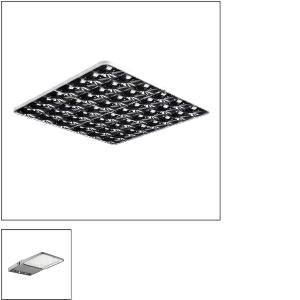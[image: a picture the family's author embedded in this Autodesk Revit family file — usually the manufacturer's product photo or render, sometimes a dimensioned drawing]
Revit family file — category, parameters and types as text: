
# Revit family: siteco_mirrortec_r__indoor___rs05_5nw14093qc_3e65
name_source: partatom
category: Lighting Fixtures
units: mm (PartAtom-declared; Revit-internal decimal feet)

## family parameters
Cut with Voids When Loaded = No
Host = Face
Light Source = No
Part Type = Normal
Room Calculation Point = No
Round Connector Dimension = Use Diameter
Shared = No

## types (1)
- 5XA7682G2H2AC (1 x LED, 33940 lm, 305.7 W, 4000K)
    Apparent Load = 306 VA
    CIE Flux Codes = 47 83 98 53 100
    Color Rendering = 70
    Color Temperature = 4000K
    Default Elevation = 1800 mm
    Description = secondary reflector, for Siteco Mirrortec® Indoor, wire hanger, housing, square, of aluminium, coated, metallic grey (RAL 9006), fresnel reflector 100, of PMMA, aluminized, highly specular, light point resolution, fresnel structure, length: 1.200 mm, width: 1.200 mm

Light Distribution: RS05
    Height = 12 mm  [stored 0.0393701 ft]
    Lamp = 1 x LED
    Lamp Light Flux = 33940 lm
    Lamp Power = 305.7 W
    Lamp count = 1
    Length = 1221 mm
    Luminous efficacy = 111 lm/W
    Manufacturer = Siteco
    ModVariant = No
    Model = 5NW14093QC
    Mounting Place = Ceiling
    Mounting Type = Pendant
    Number of Poles = 1
    OnlyDefault = Yes
    Power Factor = 1
    Product Name = Siteco Mirrortec® Indoor | RS05
    Product group = secondary reflector
    ProductGroupID = 908
    Protection Class = Protection class II
    Protection Degree = IP 66
    RLX_Detail_Level = 1
    RLX_Emergency_Light_Flux = 0 lm
    RLX_Emergency_Type = 0
    RLX_Emergency_Type_DB = No
    RlxData = <blob elided: 123869 chars, md5=4a497d8f>
    Socket = socket
    Standby Power = 0 W
    System Light Flux = 33939 lm
    System Power = 306 W
    Type Comments = Floodlight FL 20 midi, floodlight, primary light control with lens, of plastic, primary optical cover: protective disc, of toughened safety glass, transparent, light distribution: RS05, light emission: direct distribution, primary light characteristic: rotationally symmetric, installation type: surface-mounted, LED, High Power LED, rated luminous flux: 38.380lm, luminous efficacy: 126lm/W, light colour: 740, colour temperature: 4000K, control gear: ECG Plus, control: overheat protection, power reduction, digital communication interface, time-dependent luminous flux control, flexible luminous flux parameterisation, electronic power reduction, with terminal, 10-pole, max. 2.5mm², mains connection: 220..240V, AC, 50/60Hz, rated input power: 306W, LED unit, of diecast aluminium, powder-coated, Siteco® metallic grey (DB 702S), corrosivity category C5 mid according to DIN EN ISO 12944, length: 731mm, width: 450mm, height: 76mm, housing frame, of diecast aluminium, powder-coated, Siteco® metallic grey (DB 702S), wall fastening, DALI, protection rating (complete): IP66, insulation class (complete): insulation class II (safety insulation), certification: CE, ENEC, VDE, protection symbol: D, permissible operating ambient temperature: -40..+40°C, permissible operating ambient temperature for outdoor applications: -40..+50°C, standard: DIN EN 12944, packaging unit: 1 piece

individual setting: distance floodlight mirror = 3,5m / reflector tilt = 5°
    Type Image = l_577132_1005944.jpg
    URL = http://relux.com
    VarID = 5xa7682g2h2ac@adj_135665
    Voltage = 0 V
    Weight = 0.00 kg
    Width = 1221 mm

note: [stored X ft] marks values corroborated as IEEE doubles in the binary element streams (Revit-internal decimal feet)

## geometry (parser evidence)
native form markers: Blend x4, Sweep x11
no freeform markers — native parametric forms only
